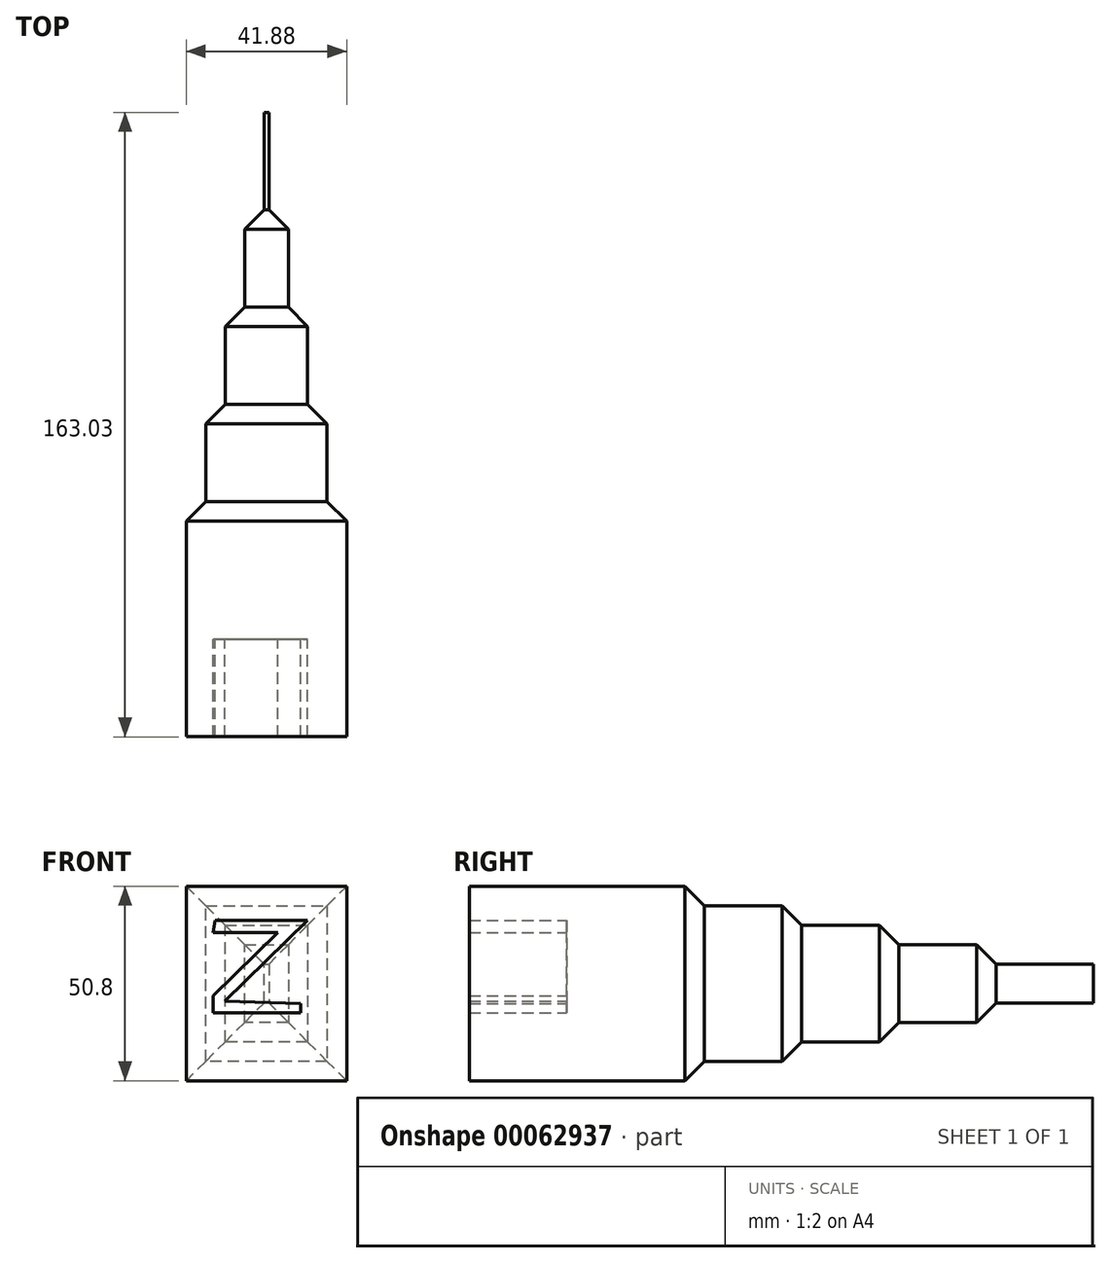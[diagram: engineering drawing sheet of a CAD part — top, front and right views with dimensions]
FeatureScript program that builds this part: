
annotation { "Feature Type Name" : "Feature", "Feature Type Description" : "" }
export const myFeature = defineFeature(function(context is Context, id is Id, definition is map)
    precondition{}
    {
        {
            var Q0;
            Q0=qCreatedBy(makeId("Top.planeOp"),FACE);
            var sketch = newSketch(context, id + "F0", { "sketchPlane" : qUnion([Q0])});
            skLineSegment(sketch, "E0", {"start": v(-17.75, 15.7) * mm, "end": v(24.13, 15.7) * mm});
            skLineSegment(sketch, "E1", {"start": v(24.13, 15.7) * mm, "end": v(24.13, -20.32) * mm});
            skLineSegment(sketch, "E2", {"start": v(24.13, -20.32) * mm, "end": v(-17.75, -20.32) * mm});
            skLineSegment(sketch, "E3", {"start": v(-17.75, -20.32) * mm, "end": v(-17.75, 15.7) * mm});
            skSolve(sketch);
        }
        {
            var Q0;
            Q0=makeQuery(id+"F0.imprint","IMPRINT",FACE,{"disambiguationData":[TD([[makeQuery(id+"F0.imprint","IMPRINT",EDGE,{"derivedFrom":sQuery(id+"F0.wireOp",EDGE,"E0")}),-1.0]])]});
            extrude(context, id + "F1", {"entities" : qUnion([Q0]), "depth" : 25.4 * mm});
        }
        {
            var Q0;
            Q0=makeQuery(id+"F1.opExtrude","CAP_FACE",FACE,{"disambiguationData":[OSD([sQuery(id+"F0.wireOp",EDGE,"E0"),sQuery(id+"F0.wireOp",EDGE,"E1"),sQuery(id+"F0.wireOp",EDGE,"E2"),sQuery(id+"F0.wireOp",EDGE,"E3")])],"isStart":false});
            var sketch = newSketch(context, id + "F2", { "sketchPlane" : qUnion([Q0])});
            skLineSegment(sketch, "E4", {"start": v(-8.21, 8.2) * mm, "end": v(15.26, 8.2) * mm, "construction": true});
            skLineSegment(sketch, "E5", {"start": v(15.26, 8.2) * mm, "end": v(-4.64, -8.07) * mm, "construction": true});
            skLineSegment(sketch, "E6", {"start": v(-4.64, -8.07) * mm, "end": v(14.18, -8.07) * mm, "construction": true});
            skLineSegment(sketch, "E7", {"start": v(14.18, -8.07) * mm, "end": v(14.18, -14.49) * mm, "construction": true});
            skLineSegment(sketch, "E8", {"start": v(14.18, -14.49) * mm, "end": v(-11.48, -14.49) * mm, "construction": true});
            skLineSegment(sketch, "E9", {"start": v(-11.48, -14.49) * mm, "end": v(-11.48, -6.66) * mm, "construction": true});
            skLineSegment(sketch, "E10", {"start": v(-11.48, -6.66) * mm, "end": v(0, 2.72) * mm, "construction": true});
            skLineSegment(sketch, "E11", {"start": v(0, 2.72) * mm, "end": v(-12.44, 2.72) * mm, "construction": true});
            skLineSegment(sketch, "E12", {"start": v(-12.44, 2.72) * mm, "end": v(-12.44, 8.2) * mm, "construction": true});
            skLineSegment(sketch, "E13", {"start": v(-12.44, 8.2) * mm, "end": v(-8.21, 8.2) * mm, "construction": true});
            skSolve(sketch);
        }
        {
            var Q0;
            Q0=makeQuery(id+"F2.imprint","IMPRINT",FACE,{"disambiguationData":[TD([[makeQuery(id+"F2.imprint","IMPRINT",EDGE,{"derivedFrom":makeQuery(id+"F1.opExtrude","CAP_EDGE",EDGE,{"disambiguationData":[OSD([sQuery(id+"F0.wireOp",EDGE,"E0")])],"isStart":false})}),-1.0]])]});
            extrude(context, id + "F3", {"entities" : qUnion([Q0]), "operationType" : NewBodyOperationType.ADD, "depth" : 25.4 * mm});
        }
        {
            var Q0;
            {var subQ0=sQuery(id+"F0.wireOp",EDGE,"E0");Q0=makeQuery(id+"F3.boolean.opBoolean","MERGE",FACE,{"derivedFrom":[makeQuery(id+"F1.opExtrude","SWEPT_FACE",FACE,{"disambiguationData":[OSD([subQ0])]}),makeQuery(id+"F3.opExtrude","SWEPT_FACE",FACE,{"disambiguationData":[OSD([subQ0])]})]});}
            chamfer(context, id + "F4", {"entities" : qUnion([Q0]), "width" : 5.08 * mm, "tangentPropagation" : true});
        }
        {
            var Q0;
            {var subQ0=sQuery(id+"F0.wireOp",EDGE,"E2");Q0=makeQuery(id+"F3.boolean.opBoolean","MERGE",FACE,{"derivedFrom":[makeQuery(id+"F1.opExtrude","SWEPT_FACE",FACE,{"disambiguationData":[OSD([subQ0])]}),makeQuery(id+"F3.opExtrude","SWEPT_FACE",FACE,{"disambiguationData":[OSD([subQ0])]})]});}
            var sketch = newSketch(context, id + "F5", { "sketchPlane" : qUnion([Q0])});
            skLineSegment(sketch, "E14", {"start": v(-10.25, 41.84) * mm, "end": v(13.9, 41.84) * mm});
            skLineSegment(sketch, "E15", {"start": v(13.9, 41.84) * mm, "end": v(-7.66, 20.79) * mm});
            skLineSegment(sketch, "E16", {"start": v(-7.66, 20.79) * mm, "end": v(12.09, 20.18) * mm});
            skLineSegment(sketch, "E17", {"start": v(12.09, 20.18) * mm, "end": v(12.09, 17.71) * mm});
            skLineSegment(sketch, "E18", {"start": v(12.09, 17.71) * mm, "end": v(-10.7, 17.71) * mm});
            skLineSegment(sketch, "E19", {"start": v(-10.7, 17.71) * mm, "end": v(-10.7, 22.2) * mm});
            skLineSegment(sketch, "E20", {"start": v(-10.7, 22.2) * mm, "end": v(6.16, 38.66) * mm});
            skLineSegment(sketch, "E21", {"start": v(6.16, 38.66) * mm, "end": v(-10.7, 38.66) * mm});
            skLineSegment(sketch, "E22", {"start": v(-10.7, 38.66) * mm, "end": v(-10.25, 41.84) * mm});
            skSolve(sketch);
        }
        {
            var Q0;
            Q0=makeQuery(id+"F5.imprint","IMPRINT",FACE,{"disambiguationData":[TD([[makeQuery(id+"F5.imprint","IMPRINT",EDGE,{"derivedFrom":sQuery(id+"F5.wireOp",EDGE,"E14")}),1.0]])]});
            extrude(context, id + "F6", {"entities" : qUnion([Q0]), "operationType" : NewBodyOperationType.ADD, "depth" : 25.4 * mm});
        }
        {
            var Q0;
            {var subQ0=sQuery(id+"F0.wireOp",EDGE,"E0");Q0=makeQuery(id+"F3.boolean.opBoolean","MERGE",FACE,{"derivedFrom":[makeQuery(id+"F1.opExtrude","SWEPT_FACE",FACE,{"disambiguationData":[OSD([subQ0])]}),makeQuery(id+"F3.opExtrude","SWEPT_FACE",FACE,{"disambiguationData":[OSD([subQ0])]})]});}
            extrude(context, id + "F7", {"entities" : qUnion([Q0]), "operationType" : NewBodyOperationType.ADD, "depth" : 25.4 * mm});
        }
        {
            var Q0;
            Q0=makeQuery(id+"F7.opExtrude","CAP_FACE",FACE,{"disambiguationData":[OSD([sQuery(id+"F0.wireOp",EDGE,"E0")])],"isStart":false});
            chamfer(context, id + "F8", {"entities" : qUnion([Q0]), "width" : 5.08 * mm, "tangentPropagation" : true});
        }
        {
            var Q0;
            Q0=makeQuery(id+"F7.opExtrude","CAP_FACE",FACE,{"disambiguationData":[OSD([sQuery(id+"F0.wireOp",EDGE,"E0")])],"isStart":false});
            extrude(context, id + "F9", {"entities" : qUnion([Q0]), "operationType" : NewBodyOperationType.ADD, "depth" : 25.4 * mm});
        }
        {
            var Q0;
            Q0=makeQuery(id+"F9.opExtrude","CAP_FACE",FACE,{"disambiguationData":[OSD([sQuery(id+"F0.wireOp",EDGE,"E0")])],"isStart":false});
            chamfer(context, id + "F10", {"entities" : qUnion([Q0]), "width" : 5.08 * mm, "tangentPropagation" : true});
        }
        {
            var Q0;
            Q0=makeQuery(id+"F9.opExtrude","CAP_FACE",FACE,{"disambiguationData":[OSD([sQuery(id+"F0.wireOp",EDGE,"E0")])],"isStart":false});
            extrude(context, id + "F11", {"entities" : qUnion([Q0]), "operationType" : NewBodyOperationType.ADD, "depth" : 25.4 * mm});
        }
        {
            var Q0;
            Q0=makeQuery(id+"F11.opExtrude","CAP_FACE",FACE,{"disambiguationData":[OSD([sQuery(id+"F0.wireOp",EDGE,"E0")])],"isStart":false});
            chamfer(context, id + "F12", {"entities" : qUnion([Q0]), "width" : 5.08 * mm, "tangentPropagation" : true});
        }
        {
            var Q0;
            Q0=makeQuery(id+"F11.opExtrude","CAP_FACE",FACE,{"disambiguationData":[OSD([sQuery(id+"F0.wireOp",EDGE,"E0")])],"isStart":false});
            extrude(context, id + "F13", {"entities" : qUnion([Q0]), "operationType" : NewBodyOperationType.ADD, "depth" : 25.4 * mm});
        }
    });
